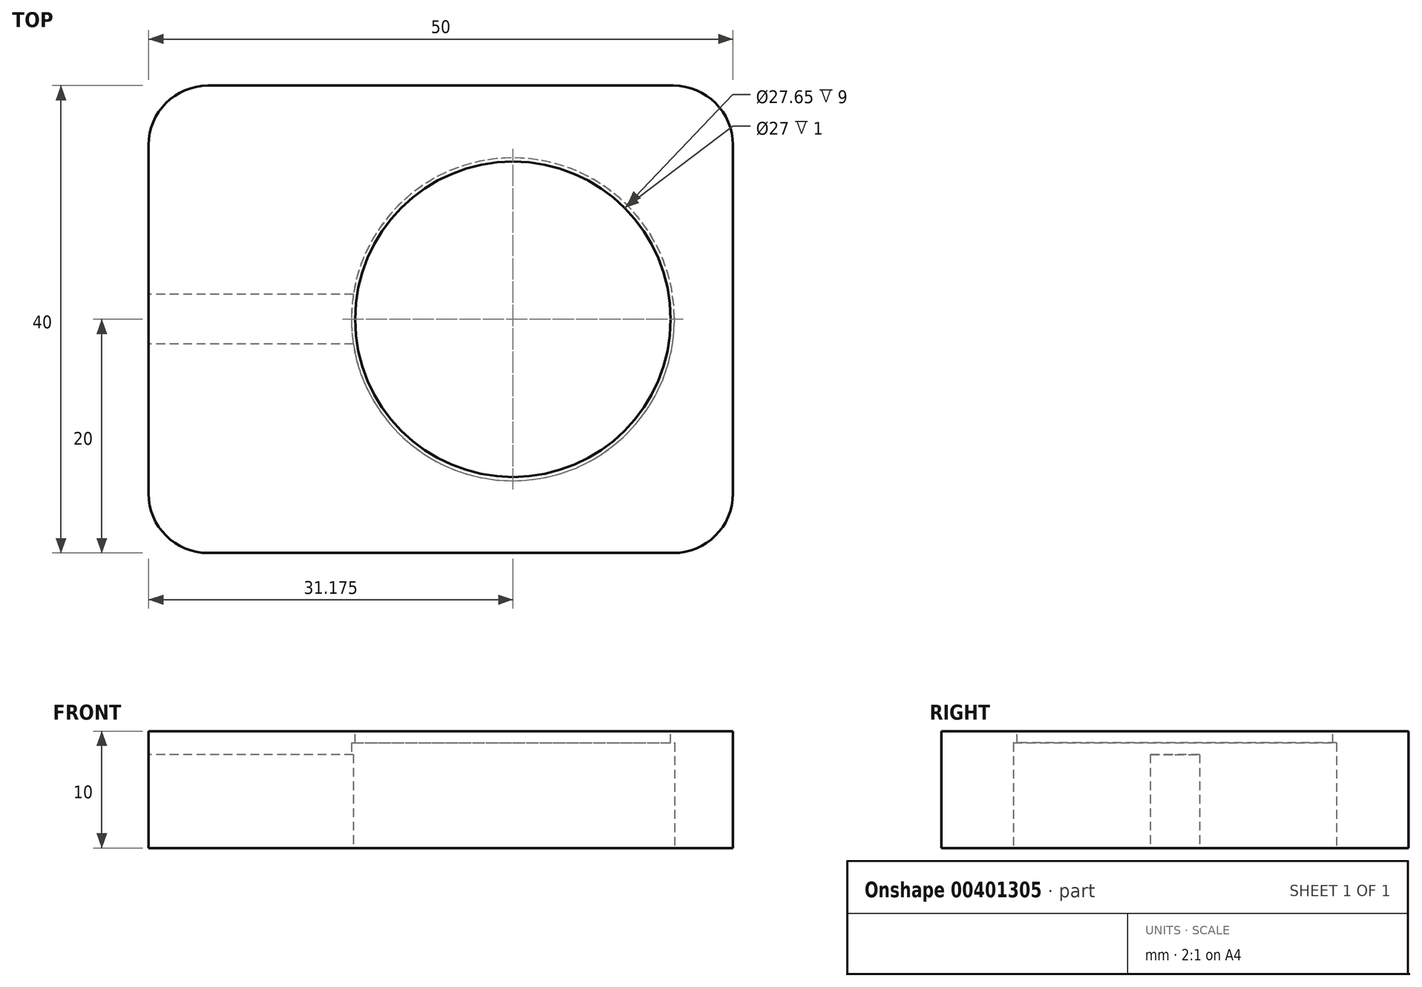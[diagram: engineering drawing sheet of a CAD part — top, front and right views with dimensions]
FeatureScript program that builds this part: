
annotation { "Feature Type Name" : "Feature", "Feature Type Description" : "" }
export const myFeature = defineFeature(function(context is Context, id is Id, definition is map)
    precondition{}
    {
        {
            var Q0;
            Q0=qCreatedBy(makeId("Top.planeOp"),FACE);
            var sketch = newSketch(context, id + "F0", { "sketchPlane" : qUnion([Q0])});
            skLineSegment(sketch, "E0.bottom", {"start": v(25, 20) * mm, "end": v(-25, 20) * mm});
            skLineSegment(sketch, "E0.top", {"start": v(25, -20) * mm, "end": v(-25, -20) * mm});
            skLineSegment(sketch, "E0.left", {"start": v(25, 20) * mm, "end": v(25, -20) * mm});
            skLineSegment(sketch, "E0.right", {"start": v(-25, 20) * mm, "end": v(-25, -20) * mm});
            skPoint(sketch, "E0.middle", {"position": v(0, 0) * mm});
            skSolve(sketch);
        }
        {
            var Q0;
            Q0=qSketchRegion(id+"F0",true);
            extrude(context, id + "F1", {"entities" : qUnion([Q0]), "depth" : 10 * mm});
        }
        {
            var Q0;
            Q0=makeQuery(id+"F1.opExtrude","CAP_FACE",FACE,{"disambiguationData":[OSD([sQuery(id+"F0.wireOp",EDGE,"E0.bottom"),sQuery(id+"F0.wireOp",EDGE,"E0.top"),sQuery(id+"F0.wireOp",EDGE,"E0.left"),sQuery(id+"F0.wireOp",EDGE,"E0.right")])],"isStart":true});
            var sketch = newSketch(context, id + "F2", { "sketchPlane" : qUnion([Q0])});
            skCircle(sketch, "E1", {"center": v(6.18, 0) * mm, "radius": 13.82 * mm});
            skSolve(sketch);
        }
        {
            var Q0;
            Q0=qSketchRegion(id+"F2",true);
            extrude(context, id + "F3", {"entities" : qUnion([Q0]), "operationType" : NewBodyOperationType.REMOVE, "oppositeDirection" : true, "depth" : 9 * mm});
        }
        {
            var Q0;
            Q0=makeQuery(id+"F1.opExtrude","CAP_FACE",FACE,{"disambiguationData":[OSD([sQuery(id+"F0.wireOp",EDGE,"E0.bottom"),sQuery(id+"F0.wireOp",EDGE,"E0.top"),sQuery(id+"F0.wireOp",EDGE,"E0.left"),sQuery(id+"F0.wireOp",EDGE,"E0.right")])],"isStart":false});
            var sketch = newSketch(context, id + "F4", { "sketchPlane" : qUnion([Q0])});
            skCircle(sketch, "E2", {"center": v(6.18, 0) * mm, "radius": 13.5 * mm});
            skSolve(sketch);
        }
        {
            var Q0;
            Q0=qSketchRegion(id+"F4",true);
            extrude(context, id + "F5", {"entities" : qUnion([Q0]), "operationType" : NewBodyOperationType.REMOVE, "endBound" : BoundingType.UP_TO_NEXT, "oppositeDirection" : true, "depth" : 25.4 * mm});
        }
        {
            var Q0;
            Q0=makeQuery(id+"F1.opExtrude","SWEPT_FACE",FACE,{"disambiguationData":[OSD([sQuery(id+"F0.wireOp",EDGE,"E0.right")])]});
            var sketch = newSketch(context, id + "F6", { "sketchPlane" : qUnion([Q0])});
            skLineSegment(sketch, "E3.bottom", {"start": v(-2.13, 8) * mm, "end": v(2.12, 8) * mm});
            skLineSegment(sketch, "E3.top", {"start": v(-2.13, 0) * mm, "end": v(2.12, 0) * mm});
            skLineSegment(sketch, "E3.left", {"start": v(-2.13, 8) * mm, "end": v(-2.13, 0) * mm});
            skLineSegment(sketch, "E3.right", {"start": v(2.12, 8) * mm, "end": v(2.12, 0) * mm});
            skLineSegment(sketch, "E4", {"start": v(-2.13, 8) * mm, "end": v(-20, 8) * mm});
            skLineSegment(sketch, "E5", {"start": v(2.12, 8) * mm, "end": v(20, 8) * mm});
            skSolve(sketch);
        }
        {
            var Q0;
            Q0=qSketchRegion(id+"F6",true);
            extrude(context, id + "F7", {"entities" : qUnion([Q0]), "operationType" : NewBodyOperationType.REMOVE, "endBound" : BoundingType.UP_TO_NEXT, "oppositeDirection" : true, "depth" : 25.4 * mm});
        }
        {
            var Q0;
            Q0=makeQuery(id+"F1.opExtrude","SWEPT_EDGE",EDGE,{"disambiguationData":[OSD([sQuery(id+"F0.wireOp",EDGE,"E0.top"),sQuery(id+"F0.wireOp",EDGE,"E0.left")])]});
            var Q1;
            Q1=makeQuery(id+"F1.opExtrude","SWEPT_EDGE",EDGE,{"disambiguationData":[OSD([sQuery(id+"F0.wireOp",EDGE,"E0.top"),sQuery(id+"F0.wireOp",EDGE,"E0.right")])]});
            var Q2;
            Q2=makeQuery(id+"F1.opExtrude","SWEPT_EDGE",EDGE,{"disambiguationData":[OSD([sQuery(id+"F0.wireOp",EDGE,"E0.bottom"),sQuery(id+"F0.wireOp",EDGE,"E0.right")])]});
            var Q3;
            Q3=makeQuery(id+"F1.opExtrude","SWEPT_EDGE",EDGE,{"disambiguationData":[OSD([sQuery(id+"F0.wireOp",EDGE,"E0.bottom"),sQuery(id+"F0.wireOp",EDGE,"E0.left")])]});
            fillet(context, id + "F8", {"entities" : qUnion([Q0, Q1, Q2, Q3]), "radius" : 5.08 * mm, "tangentPropagation" : true, "allowEdgeOverflow" : false});
        }
    });
